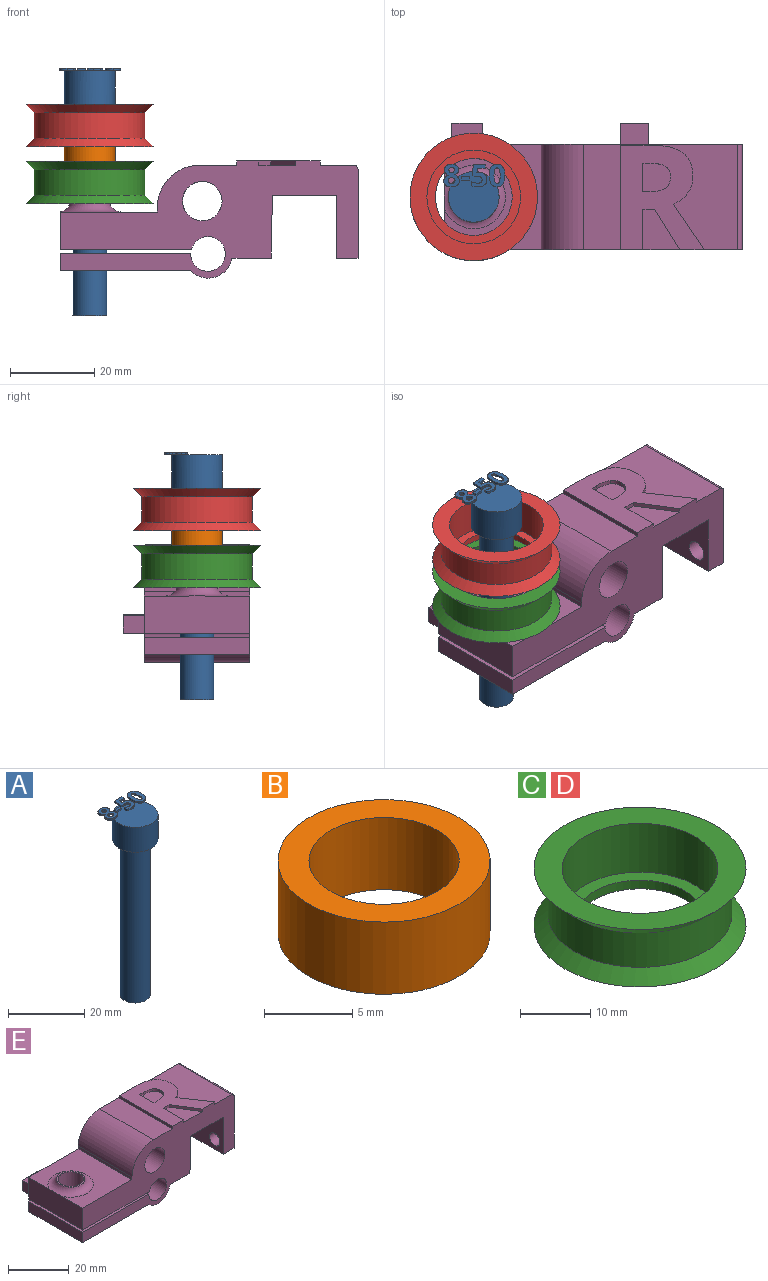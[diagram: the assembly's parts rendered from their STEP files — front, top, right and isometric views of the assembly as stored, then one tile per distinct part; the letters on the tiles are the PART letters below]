
ASSEMBLY  parts=5 mates=4
PART A: 86 faces, bbox 14.5x13.7x58.5 mm
  f0: plane 12x12mm, normal (0,0,1), area 99.4mm2, adj f5,f22,f23,f24,f25,f26,f40,f41
  f1: plane 1x0.26mm, normal (0,0,1), area 0.1mm2, adj f5,f46,f47,f48,f49
  f2: plane 0.85x0.68mm, normal (0,0,1), area 0.2mm2, adj f5,f29,f30,f31
  f3: cylinder r=4mm len=50mm, axis (0,0,-1), area 1256.6mm2, adj f4,f6
  f4: plane 8x8mm, normal (0,0,-1), area 50.3mm2, adj f3
  f5: cylinder r=6mm len=12mm, axis (0,0,-1), area 301.6mm2, adj f0,f1,f2,f6,f39,f45,f67,f85
  f6: plane 12x12mm, normal (0,0,-1), area 62.8mm2, adj f3,f5
  f7: extruded ~0.5x0.46mm, area 0.2mm2, adj f8,f37,f38,f39
  f8: extruded ~0.5x0.46mm, area 0.2mm2, adj f7,f9,f38,f39
  f9: extruded ~0.5x0.39mm, area 0.2mm2, adj f8,f10,f38,f39
  f10: extruded ~0.5x0.4mm, area 0.2mm2, adj f9,f11,f38,f39
  f11: extruded ~0.5x0.49mm, area 0.3mm2, adj f10,f12,f38,f39
  f12: extruded ~0.5x0.5mm, area 0.3mm2, adj f11,f13,f38,f39
  f13: extruded ~0.5x0.39mm, area 0.2mm2, adj f12,f37,f38,f39
  f14: extruded ~1.22x0.5mm, area 0.6mm2, adj f15,f35,f38,f39
  f15: extruded ~1.22x0.5mm, area 0.6mm2, adj f14,f16,f38,f39
  f16: extruded ~0.91x0.5mm, area 0.5mm2, adj f15,f17,f38,f39
  f17: extruded ~0.71x0.5mm, area 0.4mm2, adj f16,f18,f38,f39
  f18: extruded ~0.65x0.61mm, area 0.4mm2, adj f17,f19,f38,f39
  f19: extruded ~0.77x0.62mm, area 0.5mm2, adj f18,f20,f38,f39
  f20: extruded ~0.8x0.5mm, area 0.4mm2, adj f19,f21,f38,f39
  f21: extruded ~1.04x0.5mm, area 0.6mm2, adj f20,f22,f38,f39
  f22: extruded ~1.36x0.5mm, area 0.7mm2, adj f0,f21,f23,f38,f39
  f23: extruded ~1.33x0.5mm, area 0.7mm2, adj f0,f22,f24,f38
  f24: extruded ~1.04x0.51mm, area 0.6mm2, adj f0,f23,f25,f38
  f25: extruded ~0.75x0.5mm, area 0.4mm2, adj f0,f24,f26,f38
  f26: extruded ~0.85x0.66mm, area 0.5mm2, adj f0,f25,f27,f38,f39
  f27: extruded ~0.72x0.56mm, area 0.5mm2, adj f26,f28,f38,f39
  f28: extruded ~0.72x0.5mm, area 0.4mm2, adj f27,f35,f38,f39
  f29: extruded ~0.5x0.45mm, area 0.3mm2, adj f2,f30,f36,f38,f39
  f30: extruded ~0.5x0.47mm, area 0.3mm2, adj f2,f29,f31,f38
  f31: extruded ~0.62x0.5mm, area 0.3mm2, adj f2,f30,f32,f38,f39
  f32: extruded ~0.59x0.5mm, area 0.3mm2, adj f31,f33,f38,f39
  f33: extruded ~0.5x0.48mm, area 0.3mm2, adj f32,f34,f38,f39
  f34: extruded ~0.89x0.77mm, area 0.6mm2, adj f33,f36,f38,f39
  f35: extruded ~0.93x0.5mm, area 0.5mm2, adj f14,f28,f38,f39
  f36: extruded ~0.66x0.5mm, area 0.4mm2, adj f29,f34,f38,f39
  f37: extruded ~0.5x0.39mm, area 0.2mm2, adj f7,f13,f38,f39
  f38: plane 5.4x3.69mm, normal (0,0,1), area 12.7mm2, adj f7,f8,f9,f10,f11,f12,f13,f14
  f39: plane 5.4x3.53mm, normal (0,0,-1), area 10.2mm2, adj f5,f7,f8,f9,f10,f11,f12,f13
  f40: plane 0.9x0.5mm, normal (-1,0,0), area 0.4mm2, adj f0,f41,f43,f44
  f41: plane 1.93x0.5mm, normal (0,-1,0), area 1mm2, adj f0,f40,f42,f44
  f42: plane 0.9x0.5mm, normal (1,0,0), area 0.4mm2, adj f0,f41,f43,f44
  f43: plane 1.93x0.5mm, normal (0,1,0), area 1mm2, adj f0,f40,f42,f44
  f44: plane 1.93x0.9mm, normal (0,0,1), area 1.7mm2, adj f40,f41,f42,f43
  f45: plane 0.76x0.31mm, normal (0,0,-1), area 0mm2, adj f5,f46
  f46: extruded ~1.21x0.5mm, area 0.7mm2, adj f0,f1,f45,f47,f65,f66
  f47: extruded ~0.54x0.5mm, area 0.3mm2, adj f1,f46,f48,f66
  f48: plane 0.5x0.13mm, normal (-0.2,0.98,0), area 0.1mm2, adj f1,f47,f49,f66
  f49: plane 1.03x0.5mm, normal (1,-0.09,0), area 0.5mm2, adj f1,f48,f50,f66,f67
  f50: plane 1.88x0.5mm, normal (0,-1,0), area 0.9mm2, adj f49,f51,f66,f67
  f51: plane 0.94x0.5mm, normal (1,0,0), area 0.5mm2, adj f50,f52,f66,f67
  f52: plane 2.85x0.5mm, normal (0,1,0), area 1.4mm2, adj f51,f53,f66,f67
  f53: plane 2.68x0.5mm, normal (-1,0.07,0), area 1.3mm2, adj f0,f52,f54,f66,f67
  f54: plane 0.5x0.44mm, normal (-0.47,-0.88,0), area 0.3mm2, adj f0,f53,f55,f66
  f55: extruded ~0.5x0.37mm, area 0.2mm2, adj f0,f54,f56,f66
  f56: extruded ~0.5x0.42mm, area 0.2mm2, adj f0,f55,f57,f66
  f57: extruded ~1.05x0.8mm, area 0.8mm2, adj f0,f56,f58,f66
  f58: extruded ~1.02x0.83mm, area 0.8mm2, adj f0,f57,f59,f66
  f59: extruded ~0.72x0.5mm, area 0.4mm2, adj f0,f58,f60,f66
  f60: extruded ~0.66x0.5mm, area 0.4mm2, adj f0,f59,f61,f66
  f61: plane 0.96x0.5mm, normal (-1,0,0), area 0.5mm2, adj f0,f60,f62,f66
  f62: extruded ~1.42x0.5mm, area 0.7mm2, adj f0,f61,f63,f66
  f63: extruded ~1.55x0.5mm, area 0.8mm2, adj f0,f62,f64,f66
  f64: extruded ~1.36x0.54mm, area 0.8mm2, adj f0,f63,f65,f66
  f65: extruded ~1.17x0.5mm, area 0.6mm2, adj f0,f46,f64,f66
  f66: plane 5.33x3.51mm, normal (0,0,1), area 10.9mm2, adj f46,f47,f48,f49,f50,f51,f52,f53
  f67: plane 2.97x1.71mm, normal (0,0,-1), area 3.5mm2, adj f5,f49,f50,f51,f52,f53
  f68: extruded ~1.39x0.5mm, area 0.7mm2, adj f69,f83,f84,f85
  f69: extruded ~1.39x0.5mm, area 0.7mm2, adj f68,f70,f84,f85
  f70: extruded ~0.56x0.5mm, area 0.4mm2, adj f69,f71,f84,f85
  f71: extruded ~0.56x0.5mm, area 0.4mm2, adj f70,f72,f84,f85
  f72: extruded ~1.39x0.5mm, area 0.7mm2, adj f71,f73,f84,f85
  f73: extruded ~1.38x0.5mm, area 0.7mm2, adj f72,f74,f84,f85
  f74: extruded ~0.56x0.5mm, area 0.4mm2, adj f73,f83,f84,f85
  f75: extruded ~2.04x0.5mm, area 1.1mm2, adj f76,f82,f84,f85
  f76: extruded ~2.02x0.5mm, area 1.1mm2, adj f75,f77,f84,f85
  f77: extruded ~1.38x0.69mm, area 0.8mm2, adj f76,f78,f84,f85
  f78: extruded ~1.38x0.66mm, area 0.8mm2, adj f77,f79,f84,f85
  f79: extruded ~2.05x0.5mm, area 1.1mm2, adj f78,f80,f84,f85
  f80: extruded ~2.02x0.5mm, area 1mm2, adj f0,f79,f81,f84,f85
  f81: extruded ~1.37x0.68mm, area 0.8mm2, adj f0,f80,f82,f84
  f82: extruded ~1.39x0.66mm, area 0.8mm2, adj f0,f75,f81,f84,f85
  f83: extruded ~0.56x0.5mm, area 0.4mm2, adj f68,f74,f84,f85
  f84: plane 5.41x3.68mm, normal (0,0,1), area 12.1mm2, adj f68,f69,f70,f71,f72,f73,f74,f75
  f85: plane 5.41x3.68mm, normal (0,0,-1), area 10.3mm2, adj f5,f68,f69,f70,f71,f72,f73,f74
PART B: 4 faces, bbox 12x12x5 mm
  f0: cylinder r=4.25mm len=8.5mm, axis (0,0,-1), area 133.5mm2, adj f2,f3
  f1: cylinder r=6mm len=12mm, axis (0,0,-1), area 188.5mm2, adj f2,f3
  f2: plane 12x12mm, normal (0,0,1), area 56.4mm2, adj f0,f1
  f3: plane 12x12mm, normal (0,0,-1), area 56.4mm2, adj f0,f1
PART C: 8 faces, bbox 30.2x30.2x10 mm
  f0: plane 30.2x30.2mm, normal (0,0,1), area 329.2mm2, adj f1,f7
  f1: cylinder r=11.1mm len=22.2mm, axis (0,0,-1), area 592.8mm2, adj f0,f2
  f2: plane 22.2x22.2mm, normal (0,0,1), area 126.9mm2, adj f1,f3
  f3: cylinder r=9.1mm len=18.2mm, axis (0,0,-1), area 85.8mm2, adj f2,f4
  f4: plane 30.2x30.2mm, normal (0,0,-1), area 456.2mm2, adj f3,f5
  f5: cone r=13.1mm half-angle=45deg, axis (0,0,-1), area 250.6mm2, adj f4,f6
  f6: cylinder r=13.1mm len=26.2mm, axis (0,0,-1), area 493.9mm2, adj f5,f7
  f7: cone r=15.1mm half-angle=45deg, axis (0,0,1), area 250.6mm2, adj f0,f6
PART D: same geometry as C
PART E: 56 faces, bbox 74x30x27.7 mm
  f0: plane 36.52x25mm, normal (0,0,1), area 519.6mm2, adj f14,f15,f25,f27,f40,f41,f42,f43
  f1: plane 9.51x8.71mm, normal (0,0,1), area 54.7mm2, adj f14,f37,f38,f39
  f2: plane 25x4.12mm, normal (-1,0,0), area 103mm2, adj f5,f14,f15,f19
  f3: cylinder r=4.17mm len=8.35mm, axis (0,0,1), area 108.1mm2, adj f5,f19
  f4: plane 25x9.34mm, normal (0,0,-1), area 233.4mm2, adj f13,f14,f15,f17
  f5: plane 30.88x25mm, normal (0,0,-1), area 717.2mm2, adj f2,f3,f14,f15,f17
  f6: plane 25x8.82mm, normal (-1,0,0), area 219.6mm2, adj f7,f14,f15,f20,f24
  f7: plane 25x23mm, normal (0,0,1), area 400mm2, adj f6,f8,f14,f15,f24
  f8: plane 25x1.1mm, normal (-1,0,0), area 27.5mm2, adj f7,f14,f15,f25
  f9: plane 25x21.09mm, normal (1,0,0), area 493.5mm2, adj f10,f14,f15,f22,f23,f27
  f10: plane 25x5mm, normal (0,0,-1), area 125mm2, adj f9,f11,f14,f15
  f11: plane 25x15mm, normal (-1,0,0), area 341.3mm2, adj f10,f12,f14,f15,f22,f23
  f12: plane 25x15.3mm, normal (0,0,-1), area 382.5mm2, adj f11,f13,f14,f15
  f13: plane 25x14.91mm, normal (1,0,-0.01), area 372.8mm2, adj f4,f12,f14,f15
  f14: plane 70.52x27.75mm, normal (0,-1,0), area 1034mm2, adj f0,f1,f2,f4,f5,f6,f7,f8
  f15: plane 70.52x26.75mm, normal (0,1,0), area 962.9mm2, adj f0,f2,f4,f5,f6,f7,f8,f9
  f16: cylinder r=4.17mm len=10.78mm, axis (0,0,1), area 282.8mm2, adj f20,f21
  f17: cylinder r=5.75mm len=25mm, axis (0,-1,0), area 315.9mm2, adj f4,f5,f14,f15
  f18: cylinder r=4.1mm len=25mm, axis (0,-1,0), area 618.7mm2, adj f14,f15,f19,f20
  f19: plane 30.91x25mm, normal (0,0,1), area 718.1mm2, adj f2,f3,f14,f15,f18
  f20: plane 31.07x30mm, normal (0,0,-1), area 758.4mm2, adj f6,f14,f15,f16,f18,f29,f30,f31
  f21: plane 9.35x9.35mm, normal (0,0,1), area 13.9mm2, adj f16,f24
  f22: cylinder r=2.43mm len=5mm, axis (1,0,0), area 76.2mm2, adj f9,f11
  f23: cylinder r=2.2mm len=5mm, axis (1,0,0), area 69.1mm2, adj f9,f11
  f24: torus R=7.5mm, axis (0,0,-1), area 134.6mm2, adj f6,f7,f21
  f25: cylinder r=10mm len=25mm, axis (0,-1,0), area 392.7mm2, adj f0,f8,f14,f15
  f26: cylinder r=4.68mm len=25mm, axis (0,-1,0), area 735.2mm2, adj f14,f15
  f27: cylinder r=1mm len=25mm, axis (0,-1,0), area 39.3mm2, adj f0,f9,f14,f15
  f28: plane 7.3x5mm, normal (0,0,1), area 36.5mm2, adj f15,f29,f30,f31
  f29: plane 5x4.12mm, normal (-1,0,0), area 20.6mm2, adj f15,f20,f28,f31
  f30: plane 5x4.12mm, normal (1,0,0), area 20.6mm2, adj f15,f20,f28,f31
  f31: plane 7.3x4.12mm, normal (0,1,0), area 30.1mm2, adj f20,f28,f29,f30
  f32: plane 6.63x5mm, normal (0,0,1), area 33.2mm2, adj f15,f33,f35,f36
  f33: plane 5x4.5mm, normal (-1,0,0), area 22.5mm2, adj f15,f32,f34,f36
  f34: plane 6.63x5mm, normal (0,0,-1), area 33.2mm2, adj f15,f33,f35,f36
  f35: plane 5x4.5mm, normal (1,0,0), area 22.5mm2, adj f15,f32,f34,f36
  f36: plane 6.63x4.5mm, normal (0,1,0), area 29.9mm2, adj f32,f33,f34,f35
  f37: plane 9.51x1mm, normal (1,0,0), area 9.5mm2, adj f1,f14,f38,f54
  f38: plane 2.79x1mm, normal (0,-1,0), area 2.8mm2, adj f1,f37,f39,f54
  f39: plane 9.51x5.92mm, normal (-0.85,-0.53,0), area 11.2mm2, adj f1,f14,f38,f54
  f40: extruded ~10.8x7.29mm, area 13mm2, adj f0,f14,f41,f54
  f41: extruded ~3.41x2.67mm, area 4.4mm2, adj f0,f40,f42,f54
  f42: extruded ~3.89x1.2mm, area 4.1mm2, adj f0,f41,f43,f54
  f43: extruded ~5.59x2.42mm, area 6.3mm2, adj f0,f42,f44,f54
  f44: extruded ~7.48x1.84mm, area 7.8mm2, adj f0,f43,f45,f54
  f45: plane 7.22x1mm, normal (0,1,0), area 7.2mm2, adj f0,f44,f46,f54
  f46: plane 24.79x1mm, normal (-1,0,0), area 24.8mm2, adj f0,f14,f45,f54
  f47: plane 1.69x1mm, normal (0,1,0), area 1.7mm2, adj f48,f53,f54,f55
  f48: plane 6.7x1mm, normal (1,0,0), area 6.7mm2, adj f47,f49,f54,f55
  f49: plane 1.6x1mm, normal (0,-1,0), area 1.6mm2, adj f48,f50,f54,f55
  f50: extruded ~3.75x1mm, area 3.9mm2, adj f49,f51,f54,f55
  f51: extruded ~2.51x1.21mm, area 2.9mm2, adj f50,f52,f54,f55
  f52: extruded ~2.61x1.19mm, area 3mm2, adj f51,f53,f54,f55
  f53: extruded ~3.68x1mm, area 3.8mm2, adj f47,f52,f54,f55
  f54: plane 24.79x19.8mm, normal (0,0,1), area 300mm2, adj f14,f37,f38,f39,f40,f41,f42,f43
  f55: plane 6.7x6.56mm, normal (0,0,1), area 38.8mm2, adj f47,f48,f49,f50,f51,f52,f53
PLACE A t=(-103.78,-12.5,-13.6)mm
PLACE B rot(axis=(1,0,0),180deg) t=(-103.78,-12.5,26.4)mm
PLACE C t=(-103.78,-12.5,18.1)mm
PLACE D t=(-103.78,-12.5,31.6)mm
PLACE E at identity
MATE fastened A.f3 <-> D.f1  axis (0,0,-1) through (-103.78,-12.5,36.4)mm
MATE fastened B.f0 <-> C.f1  axis (0,0,1) through (-103.78,-12.5,21.4)mm
MATE fastened C.f1 <-> E.f3  axis (0,0,-1) through (-103.78,-12.5,12.9)mm
MATE fastened D.f1 <-> B.f0  axis (0,0,-1) through (-103.78,-12.5,26.4)mm
